# Revit family: Tub-Double Bowl-Clark 45L Flushline1
name_source: partatom
category: Plumbing Fixtures
revit_build: Autodesk Revit Architecture 2012 (Build: 20110916_2132(x64)
units: mm (PartAtom-declared; Revit-internal decimal feet)

## types (1)
- Double Flushline - with By-pass
    Assembly Code = D2010420
    CW Connection = No
    Cost = 0 $
    Default Elevation = 0 mm  [stored 0 ft]
    Depth_ANZRS = 265 mm
    Description = Double 45 Litre Flushline Laundry Tubs
    HW Connection = No
    Keynote = SK
    LH ByPass = Yes
    LH ByPass Penetration = 0 mm  [stored 0 ft]
    LH Tap Penetation = 100 mm  [stored 0.328084 ft]
    LH Taphole = No
    Length_ANZRS = 1248 mm  [stored 4.09449 ft]
    Manufacturer = Clark
    Material_ANZRS = Metal-Stainless-Caroma
    Model = 8710
    RH ByPass = Yes
    RH ByPass Penetration = 0 mm  [stored 0 ft]
    RH Tap Penetation = 100 mm  [stored 0.328084 ft]
    RH Taphole = No
    Type Comments = Includes basket waste, Bowl Volume 45L, Carton size 1250 x 480 x 280, Carton weight 10.5kg, Match with Dorf Eclipse mixer range
    URL = http://www.clark.com.au
    Vent Connection = No
    WFU = 2
    Waste Connection = Yes
    Waste Radius = 30 mm  [stored 0.0984252 ft]
    Width_ANZRS = 473 mm  [stored 1.55184 ft]

note: [stored X ft] marks values corroborated as IEEE doubles in the binary element streams (Revit-internal decimal feet)

## geometry (parser evidence)
native form markers: Sweep x2
no freeform markers — native parametric forms only
